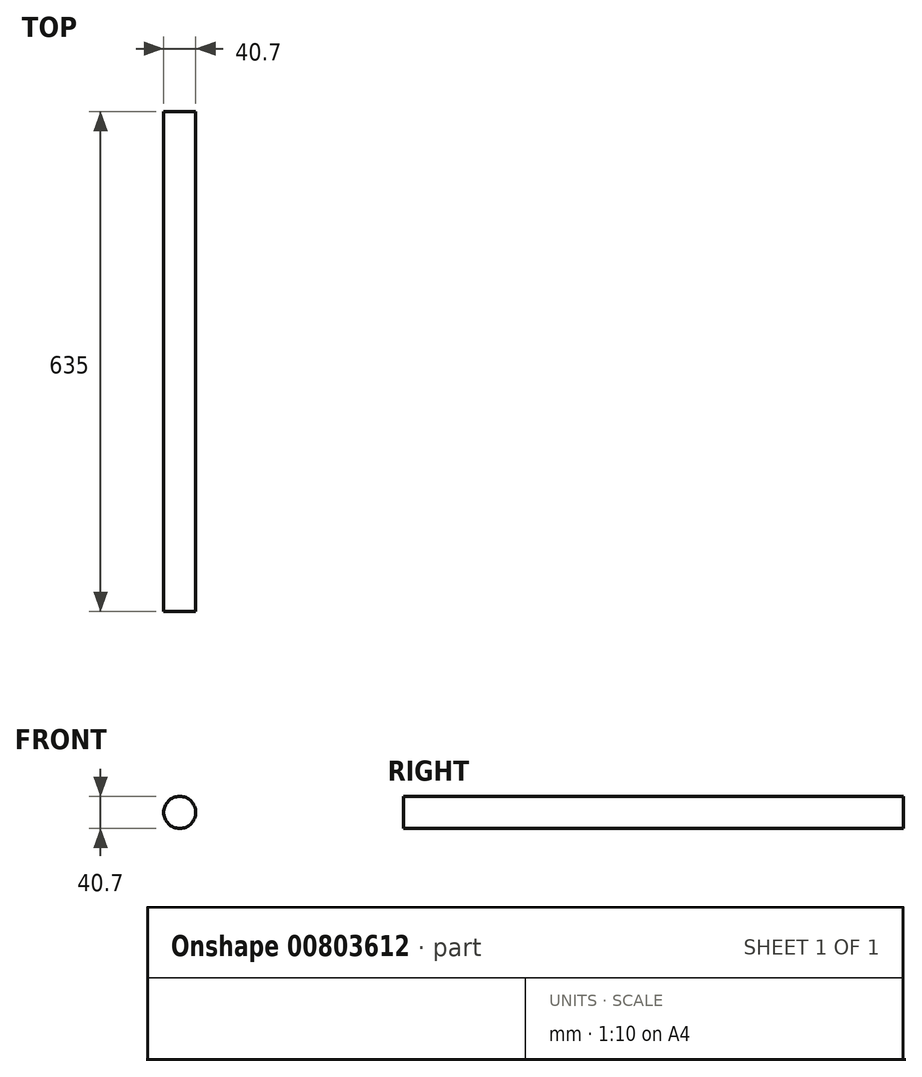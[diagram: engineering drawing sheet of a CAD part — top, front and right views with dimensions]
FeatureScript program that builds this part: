
annotation { "Feature Type Name" : "Feature", "Feature Type Description" : "" }
export const myFeature = defineFeature(function(context is Context, id is Id, definition is map)
    precondition{}
    {
        {
            var Q0;
            Q0=qCreatedBy(makeId("Front.planeOp"),FACE);
            var sketch = newSketch(context, id + "F0", { "sketchPlane" : qUnion([Q0])});
            skCircle(sketch, "E0", {"center": v(0, 0) * mm, "radius": 20.35 * mm});
            skSolve(sketch);
        }
        {
            var Q0;
            Q0 = qSketchRegion(id + "F0", true);
            extrude(context, id + "F1", {"entities" : qUnion([Q0]), "depth" : 635 * mm, "offsetDistance" : 25.4 * mm});
        }
    });
